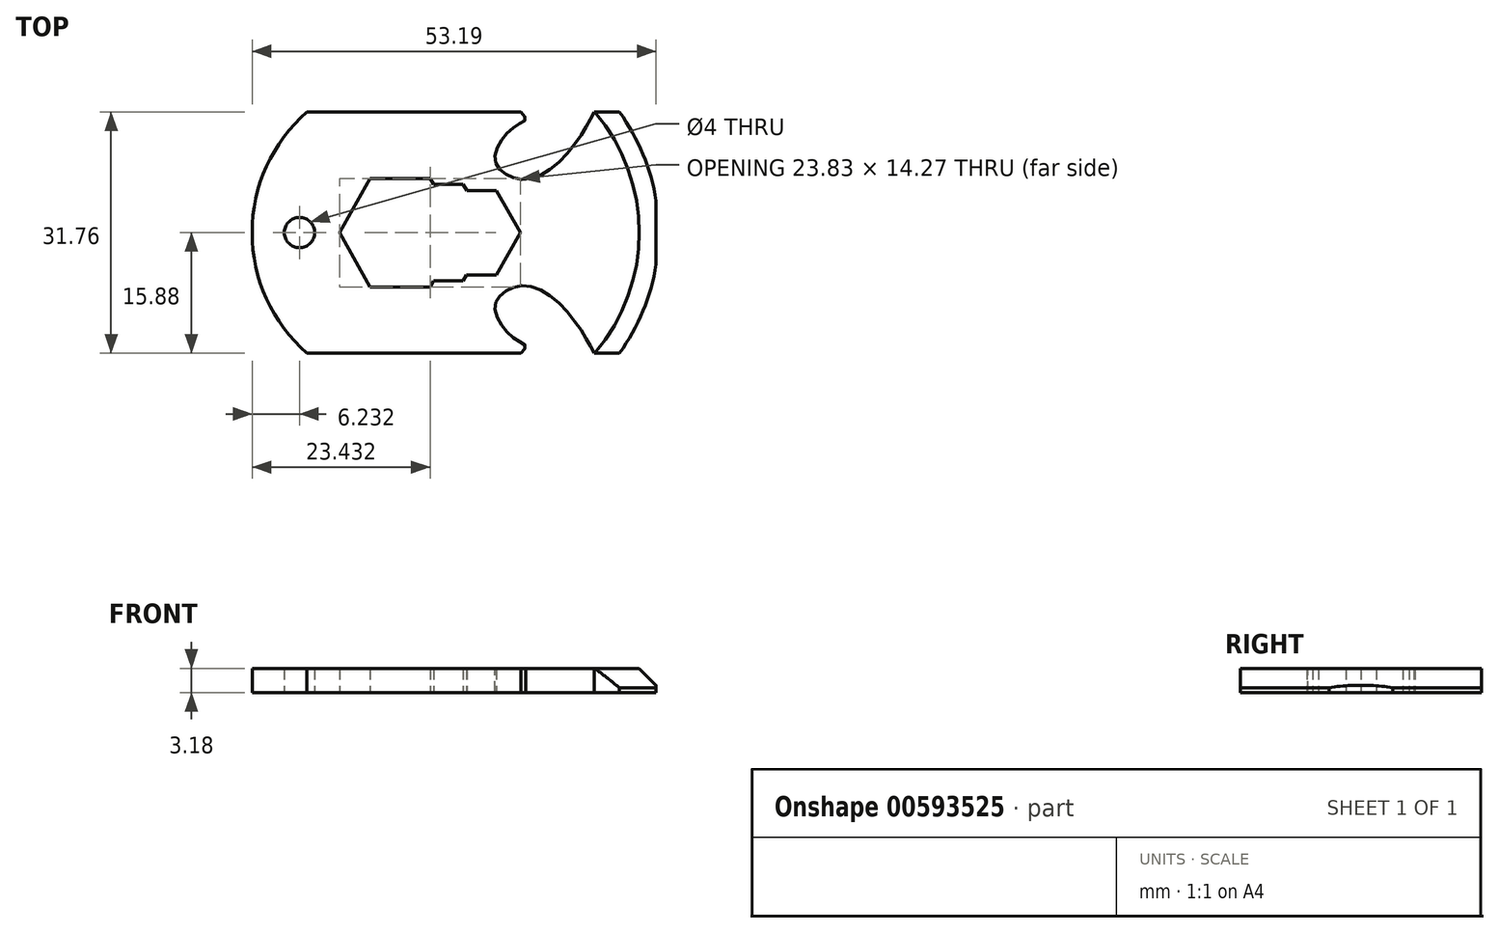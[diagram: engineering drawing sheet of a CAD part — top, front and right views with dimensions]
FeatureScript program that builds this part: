
annotation { "Feature Type Name" : "Feature", "Feature Type Description" : "" }
export const myFeature = defineFeature(function(context is Context, id is Id, definition is map)
    precondition{}
    {
        {
            var Q0;
            Q0=qCreatedBy(makeId("Top.planeOp"),FACE);
            var sketch = newSketch(context, id + "F0", { "sketchPlane" : qUnion([Q0])});
            skLineSegment(sketch, "E0.bottom", {"start": v(-25.4, 15.88) * mm, "end": v(25.4, 15.88) * mm});
            skLineSegment(sketch, "E0.top", {"start": v(-25.4, -15.87) * mm, "end": v(25.4, -15.87) * mm});
            skLineSegment(sketch, "E0.left", {"start": v(-25.4, 15.88) * mm, "end": v(-25.4, -15.87) * mm});
            skLineSegment(sketch, "E0.right", {"start": v(25.4, 15.87) * mm, "end": v(25.4, -15.87) * mm});
            skPoint(sketch, "E0.middle", {"position": v(0, 0) * mm});
            skLineSegment(sketch, "E1.MirrorCS", {"start": v(-76.2, 15.88) * mm, "end": v(-76.2, -15.87) * mm});
            skArc(sketch, "E2", {"start": v(-20.57, 15.87) * mm, "mid": v(-27.8, 0) * mm, "end": v(-20.57, -15.87) * mm});
            skArc(sketch, "E3", {"start": v(20.57, -15.87) * mm, "mid": v(25.72, 0) * mm, "end": v(20.57, 15.88) * mm});
            skCircle(sketch, "E4", {"center": v(-21.56, 0) * mm, "radius": 2 * mm});
            skLineSegment(sketch, "E5", {"start": v(-12.3, 7.14) * mm, "end": v(-16.27, 0) * mm});
            skLineSegment(sketch, "E6", {"start": v(-16.27, 0) * mm, "end": v(-12.3, -7.14) * mm});
            skLineSegment(sketch, "E7", {"start": v(-12.3, 7.14) * mm, "end": v(-4.35, 7.14) * mm});
            skLineSegment(sketch, "E8", {"start": v(-12.3, -7.14) * mm, "end": v(-4.35, -7.14) * mm});
            skLineSegment(sketch, "E9", {"start": v(-4.35, 7.14) * mm, "end": v(-3.9, 6.35) * mm});
            skLineSegment(sketch, "E10", {"start": v(-3.9, -6.35) * mm, "end": v(-4.35, -7.14) * mm});
            skLineSegment(sketch, "E11", {"start": v(-3.9, 6.35) * mm, "end": v(0, 6.35) * mm});
            skLineSegment(sketch, "E12", {"start": v(-3.9, -6.35) * mm, "end": v(0, -6.35) * mm});
            skLineSegment(sketch, "E13", {"start": v(0, 6.35) * mm, "end": v(0.46, 5.55) * mm});
            skLineSegment(sketch, "E14", {"start": v(0, -6.35) * mm, "end": v(0.46, -5.56) * mm});
            skLineSegment(sketch, "E15", {"start": v(0.46, 5.55) * mm, "end": v(4.35, 5.55) * mm});
            skLineSegment(sketch, "E16", {"start": v(0.46, -5.56) * mm, "end": v(4.34, -5.56) * mm});
            skLineSegment(sketch, "E17", {"start": v(4.35, 5.55) * mm, "end": v(7.56, 0) * mm});
            skLineSegment(sketch, "E18", {"start": v(4.34, -5.56) * mm, "end": v(7.56, 0) * mm});
            skArc(sketch, "E19", {"start": v(19.55, -15.88) * mm, "mid": v(24.54, 0) * mm, "end": v(19.55, 15.88) * mm});
            skFitSpline(sketch, "E20", {"points": [v(17.26, 15.87) * mm, v(15.73, 13.2) * mm, v(12.32, 9.02) * mm, v(8.3, 7) * mm, v(5.52, 7.77) * mm, v(4.2, 9.5) * mm, v(5.03, 12.15) * mm, v(6.97, 14.1) * mm, v(8.22, 14.93) * mm, v(7.6, 15.87) * mm], "startDerivative": vector(-11.4, -21.47) * mm, "endDerivative": vector(-14.56, 14.4) * mm});
            skFitSpline(sketch, "E21.MirrorCS", {"points": [v(17.26, -15.88) * mm, v(15.73, -13.2) * mm, v(12.32, -9.02) * mm, v(8.3, -7) * mm, v(5.52, -7.77) * mm, v(4.2, -9.5) * mm, v(5.03, -12.15) * mm, v(6.97, -14.1) * mm, v(8.22, -14.93) * mm, v(7.6, -15.88) * mm], "startDerivative": vector(-11.4, 21.47) * mm, "endDerivative": vector(-14.56, -14.4) * mm});
            skSolve(sketch);
        }
        {
            var Q0;
            {var subQ0=sQuery(id+"F0.wireOp",EDGE,"E2");var subQ1=sQuery(id+"F0.wireOp",EDGE,"E0.left");var subQ2=makeQuery(id+"F0.imprint","INTERSECT",VERTEX,{"disambiguationData":[OD(0.0)],"derivedFrom":[subQ1,subQ0]});Q0=makeQuery(id+"F0.imprint","IMPRINT",FACE,{"disambiguationData":[TD([[makeQuery(id+"F0.imprint","IMPRINT",EDGE,{"disambiguationData":[TD([[subQ2,-1.0]])],"derivedFrom":subQ1}),-1.0]])]});}
            var Q1;
            Q1=makeQuery(id+"F0.imprint","IMPRINT",FACE,{"disambiguationData":[TD([[makeQuery(id+"F0.imprint","IMPRINT",EDGE,{"derivedFrom":sQuery(id+"F0.wireOp",EDGE,"E4")}),-1.0]])]});
            var Q2;
            {var subQ0=sQuery(id+"F0.wireOp",EDGE,"E3");var subQ1=sQuery(id+"F0.wireOp",EDGE,"E0.right");var subQ2=makeQuery(id+"F0.imprint","INTERSECT",VERTEX,{"disambiguationData":[OD(0.0)],"derivedFrom":[subQ1,subQ0]});Q2=makeQuery(id+"F0.imprint","IMPRINT",FACE,{"disambiguationData":[TD([[makeQuery(id+"F0.imprint","IMPRINT",EDGE,{"disambiguationData":[TD([[subQ2,-1.0]])],"derivedFrom":subQ1}),1.0]])]});}
            var Q3;
            {var subQ5=sQuery(id+"F0.wireOp",EDGE,"E19");Q3=makeQuery(id+"F0.imprint","IMPRINT",FACE,{"disambiguationData":[TD([[makeQuery(id+"F0.imprint","IMPRINT",EDGE,{"derivedFrom":subQ5}),-1.0]])]});}
            extrude(context, id + "F1", {"entities" : qUnion([Q0, Q1, Q2, Q3]), "depth" : 3.17 * mm, "offsetDistance" : 25.4 * mm});
        }
        {
            var Q0;
            Q0=makeQuery(id+"F1.opExtrude","CAP_EDGE",EDGE,{"disambiguationData":[OSD([sQuery(id+"F0.wireOp",EDGE,"E3")])],"isStart":false});
            chamfer(context, id + "F2", {"entities" : qUnion([Q0]), "chamferType" : ChamferType.TWO_OFFSETS, "width1" : 2.54 * mm, "oppositeDirection" : false, "width2" : 2.54 * mm, "tangentPropagation" : true});
        }
    });
